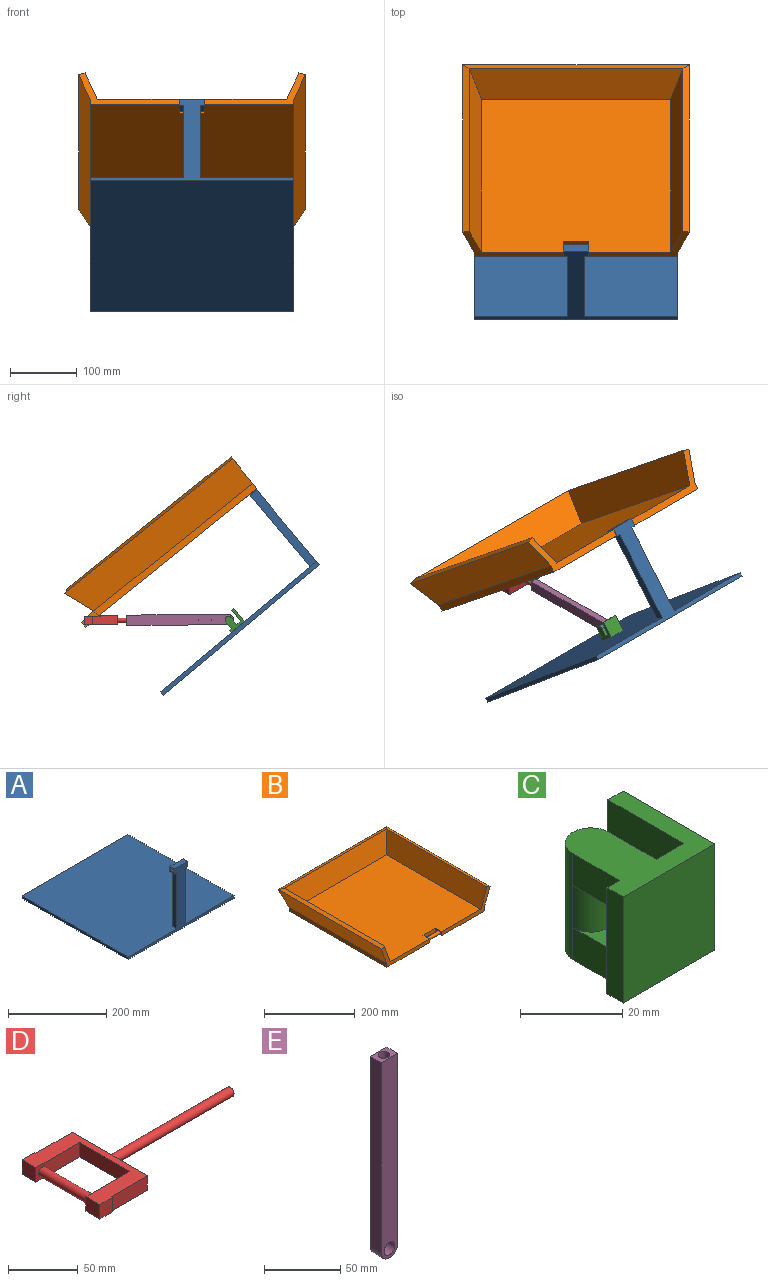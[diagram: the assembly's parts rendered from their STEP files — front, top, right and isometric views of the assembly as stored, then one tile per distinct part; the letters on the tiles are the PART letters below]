
ASSEMBLY  parts=5 mates=5
PART A: 15 faces, bbox 304.8x304.8x158.8 mm
  f0: plane 304.8x304.8mm, normal (0,0,1), area 92580.5mm2, adj f1,f2,f3,f4,f6,f7,f8
  f1: plane 304.8x158.75mm, normal (0,-1,0), area 5967.7mm2, adj f0,f2,f4,f5,f6,f8,f9,f10
  f2: plane 304.8x6.35mm, normal (1,0,0), area 1935.5mm2, adj f0,f1,f3,f5
  f3: plane 304.8x6.35mm, normal (0,1,0), area 1935.5mm2, adj f0,f2,f4,f5
  f4: plane 304.8x6.35mm, normal (-1,0,0), area 1935.5mm2, adj f0,f1,f3,f5
  f5: plane 304.8x304.8mm, normal (0,0,-1), area 92903mm2, adj f1,f2,f3,f4
  f6: plane 139.7x12.7mm, normal (1,0,0), area 1774.2mm2, adj f0,f1,f7,f9
  f7: plane 152.4x38.1mm, normal (0,1,0), area 4032.3mm2, adj f0,f6,f8,f9,f10,f11,f12,f13
  f8: plane 139.7x12.7mm, normal (-1,0,0), area 1774.2mm2, adj f0,f1,f7,f13
  f9: plane 12.7x6.35mm, normal (0,0,-1), area 80.6mm2, adj f1,f6,f7,f10
  f10: plane 12.7x12.7mm, normal (1,0,0), area 115.7mm2, adj f1,f7,f9,f12,f14
  f11: plane 12.7x12.7mm, normal (-1,0,0), area 115.7mm2, adj f1,f7,f12,f13,f14
  f12: plane 38.1x12.7mm, normal (0,0,1), area 483.9mm2, adj f1,f7,f10,f11
  f13: plane 12.7x6.35mm, normal (0,0,-1), area 80.6mm2, adj f1,f7,f8,f11
  f14: cylinder r=3.81mm len=38.1mm, axis (1,0,0), area 912.1mm2, adj f10,f11
PART B: 27 faces, bbox 339.5x330.1x63.1 mm
  f0: plane 293.99x283.18mm, normal (0,0,1), area 82476.1mm2, adj f1,f7,f8,f9,f15,f23,f24,f25
  f1: plane 150.72x61.37mm, normal (0,-1,0), area 1889.7mm2, adj f0,f5,f6,f8,f10,f12,f23
  f2: plane 127x10.16mm, normal (0,1,-0.07), area 1293.4mm2, adj f11,f12,f14,f18
  f3: plane 322.17x47.74mm, normal (-0.94,0,-0.34), area 15925.2mm2, adj f4,f9,f11,f14
  f4: plane 322.17x9.55mm, normal (-0.34,0,0.94), area 3224.8mm2, adj f3,f7,f9,f13
  f5: plane 322.17x9.55mm, normal (0.34,0,0.94), area 3224.8mm2, adj f1,f6,f8,f13
  f6: plane 322.17x47.74mm, normal (0.94,0,-0.34), area 15925.2mm2, adj f1,f5,f10,f14
  f7: plane 312.63x51.21mm, normal (0.94,0,0.34), area 16529.6mm2, adj f0,f4,f9,f15
  f8: plane 312.63x51.21mm, normal (-0.94,0,0.34), area 16529.6mm2, adj f0,f1,f5,f15
  f9: plane 150.72x61.37mm, normal (0,-1,0), area 1889.7mm2, adj f0,f3,f4,f7,f11,f12,f24
  f10: plane 304.8x10.16mm, normal (1,0,0), area 3093.2mm2, adj f1,f6,f12,f16
  f11: plane 304.8x10.16mm, normal (-1,0,0), area 3093.2mm2, adj f2,f3,f9,f12
  f12: plane 304.8x304.1mm, normal (0,0,-1), area 91915.6mm2, adj f1,f2,f9,f10,f11,f16,f17,f23
  f13: plane 339.55x9.55mm, normal (0,0.34,0.94), area 3352.8mm2, adj f4,f5,f14,f15
  f14: plane 339.55x47.74mm, normal (0,0.94,-0.34), area 16366.5mm2, adj f2,f3,f6,f13,f16,f19
  f15: plane 320.45x51.21mm, normal (0,-0.94,0.34), area 16448.3mm2, adj f0,f7,f8,f13
  f16: plane 127x10.16mm, normal (0,1,-0.07), area 1293.4mm2, adj f10,f12,f14,f20
  f17: plane 50.8x25.34mm, normal (0,-0.07,-1), area 1290.3mm2, adj f12,f18,f20,f21
  f18: plane 26.04x11.91mm, normal (-1,0,0), area 213.1mm2, adj f2,f17,f19,f21,f22
  f19: plane 50.8x25.34mm, normal (0,0.07,1), area 1290.3mm2, adj f14,f18,f20,f21
  f20: plane 26.04x11.91mm, normal (1,0,0), area 213.1mm2, adj f16,f17,f19,f21,f22
  f21: plane 50.8x10.16mm, normal (0,1,-0.07), area 517.4mm2, adj f17,f18,f19,f20
  f22: cylinder r=3.81mm len=50.8mm, axis (-1,0,0), area 1216.1mm2, adj f18,f20
  f23: plane 20.32x10.16mm, normal (-1,0,0), area 160.8mm2, adj f0,f1,f12,f25,f26
  f24: plane 20.32x10.16mm, normal (1,0,0), area 160.8mm2, adj f0,f9,f12,f25,f26
  f25: plane 38.1x10.16mm, normal (0,-1,0), area 387.1mm2, adj f0,f12,f23,f24
  f26: cylinder r=3.81mm len=38.1mm, axis (1,0,0), area 912.1mm2, adj f23,f24
PART C: 15 faces, bbox 25.4x25.4x25.4 mm
  f0: plane 25.4x25.4mm, normal (0,0,1), area 373.2mm2, adj f2,f3,f4,f5,f6,f7,f8,f9
  f1: plane 25.4x25.4mm, normal (0,0,-1), area 373.2mm2, adj f2,f3,f4,f5,f6,f7,f8,f9
  f2: plane 25.4x25.4mm, normal (0,-1,0), area 645.2mm2, adj f0,f1,f3,f5
  f3: plane 25.4x25.4mm, normal (1,0,0), area 645.2mm2, adj f0,f1,f2,f4
  f4: plane 25.4x4.2mm, normal (0,1,0), area 106.7mm2, adj f0,f1,f3,f8
  f5: plane 25.4x4.46mm, normal (-1,0,0), area 113.2mm2, adj f0,f1,f2,f6
  f6: plane 25.4x21.2mm, normal (0,1,0), area 383.6mm2, adj f0,f1,f5,f7,f8,f9,f10,f12
  f7: plane 25.4x12.9mm, normal (1,0,0), area 196.9mm2, adj f0,f1,f6,f10,f11,f12,f13
  f8: plane 25.4x20.94mm, normal (-1,0,0), area 531.9mm2, adj f0,f1,f4,f6
  f9: plane 25.4x12.99mm, normal (-1,0,0), area 199.1mm2, adj f0,f1,f6,f10,f12,f13,f14
  f10: plane 12.89x10.16mm, normal (0,0,-1), area 90.9mm2, adj f6,f7,f9,f11,f14
  f11: plane 10.16x0mm, normal (0,-1,0), area 0mm2, adj f7,f10,f12,f14
  f12: plane 12.89x10.16mm, normal (0,0,1), area 90.9mm2, adj f6,f7,f9,f11,f14
  f13: cylinder r=5.08mm len=25.4mm, axis (0,0,1), area 404.9mm2, adj f0,f1,f7,f9
  f14: cylinder r=5.08mm len=10.16mm, axis (0,0,1), area 161mm2, adj f9,f10,f11,f12
PART D: 17 faces, bbox 171.5x78.7x12.7 mm
  f0: cylinder r=3.81mm len=50.8mm, axis (0,1,0), area 1216.1mm2, adj f6,f10
  f1: plane 78.74x49.53mm, normal (0,0,-1), area 1548.4mm2, adj f2,f4,f5,f6,f7,f8,f9,f10
  f2: plane 12.7x1.27mm, normal (1,0,0), area 16.1mm2, adj f1,f3,f5,f11
  f3: plane 78.74x49.53mm, normal (0,0,1), area 1548.4mm2, adj f2,f4,f5,f6,f7,f8,f9,f10
  f4: plane 13.97x12.7mm, normal (-1,0,0), area 177.4mm2, adj f1,f3,f5,f6
  f5: plane 12.7x12.7mm, normal (0,-1,0), area 161.3mm2, adj f1,f2,f3,f4
  f6: plane 44.45x12.7mm, normal (0,1,0), area 518.9mm2, adj f0,f1,f3,f4,f13
  f7: plane 13.97x12.7mm, normal (-1,0,0), area 177.4mm2, adj f1,f3,f9,f10
  f8: plane 12.7x1.27mm, normal (1,0,0), area 16.1mm2, adj f1,f3,f9,f16
  f9: plane 12.7x12.7mm, normal (0,1,0), area 161.3mm2, adj f1,f3,f7,f8
  f10: plane 44.45x12.7mm, normal (0,-1,0), area 518.9mm2, adj f0,f1,f3,f7,f13
  f11: plane 36.83x12.7mm, normal (0,-1,0), area 467.7mm2, adj f1,f2,f3,f12
  f12: plane 76.2x12.7mm, normal (1,0,0), area 922.1mm2, adj f1,f3,f11,f14,f16
  f13: plane 50.8x12.7mm, normal (-1,0,0), area 645.2mm2, adj f1,f3,f6,f10
  f14: cylinder r=3.81mm len=121.92mm, axis (-1,0,0), area 2918.6mm2, adj f12,f15
  f15: plane 7.62x7.62mm, normal (1,0,0), area 45.6mm2, adj f14
  f16: plane 36.83x12.7mm, normal (0,1,0), area 467.7mm2, adj f1,f3,f8,f12
PART E: 9 faces, bbox 15.2x10.2x160 mm
  f0: cylinder r=7.62mm len=15.24mm, axis (0,1,0), area 243.2mm2, adj f1,f4,f5,f6
  f1: plane 152.4x10.16mm, normal (1,0,0), area 1548.4mm2, adj f0,f2,f5,f6
  f2: plane 15.24x10.16mm, normal (0,0,1), area 109.2mm2, adj f1,f4,f5,f6,f7
  f3: cylinder r=5.08mm len=10.16mm, axis (0,1,0), area 324.3mm2, adj f5,f6
  f4: plane 152.4x10.16mm, normal (-1,0,0), area 1548.4mm2, adj f0,f2,f5,f6
  f5: plane 160.02x15.24mm, normal (0,-1,0), area 2332.7mm2, adj f0,f1,f2,f3,f4
  f6: plane 160.02x15.24mm, normal (0,1,0), area 2332.7mm2, adj f0,f1,f2,f3,f4
  f7: cylinder r=3.81mm len=127mm, axis (0,0,1), area 3040.2mm2, adj f2,f8
  f8: plane 7.62x7.62mm, normal (0,0,1), area 45.6mm2, adj f7
PLACE A rot(axis=(-1,0,0),39.9deg) t=(44.37,-121.06,243.06)mm fixed
PLACE B rot(axis=(-1,0,0),38.8deg) t=(44.37,-27.56,356.72)mm
PLACE C rot(axis=(0.39,-0.83,-0.39),100.3deg) t=(-95.33,8.48,159.6)mm
PLACE D rot(axis=(0.71,-0.71,0),179.8deg) t=(-108.03,224.23,159.75)mm
PLACE E rot(axis=(-0.58,-0.58,-0.58),120.1deg) t=(-102.95,14.68,160.53)mm
MATE revolute B.f26 <-> A.f14  axis (1,0,0) through (-127.08,-18.43,355.91)mm
MATE fastened C.f2 <-> A.f0  axis (0,-0.64,-0.77) through (-108.03,0.33,149.86)mm
MATE slider D.f14 <-> E.f7  axis (0,-1,0) through (-108.03,59.13,160.37)mm
MATE revolute D.f0 <-> B.f22  axis (-1,0,0) through (-133.43,224.23,159.75)mm
MATE revolute E.f3 <-> C.f13  axis (1,0,0) through (-113.11,14.68,160.53)mm
